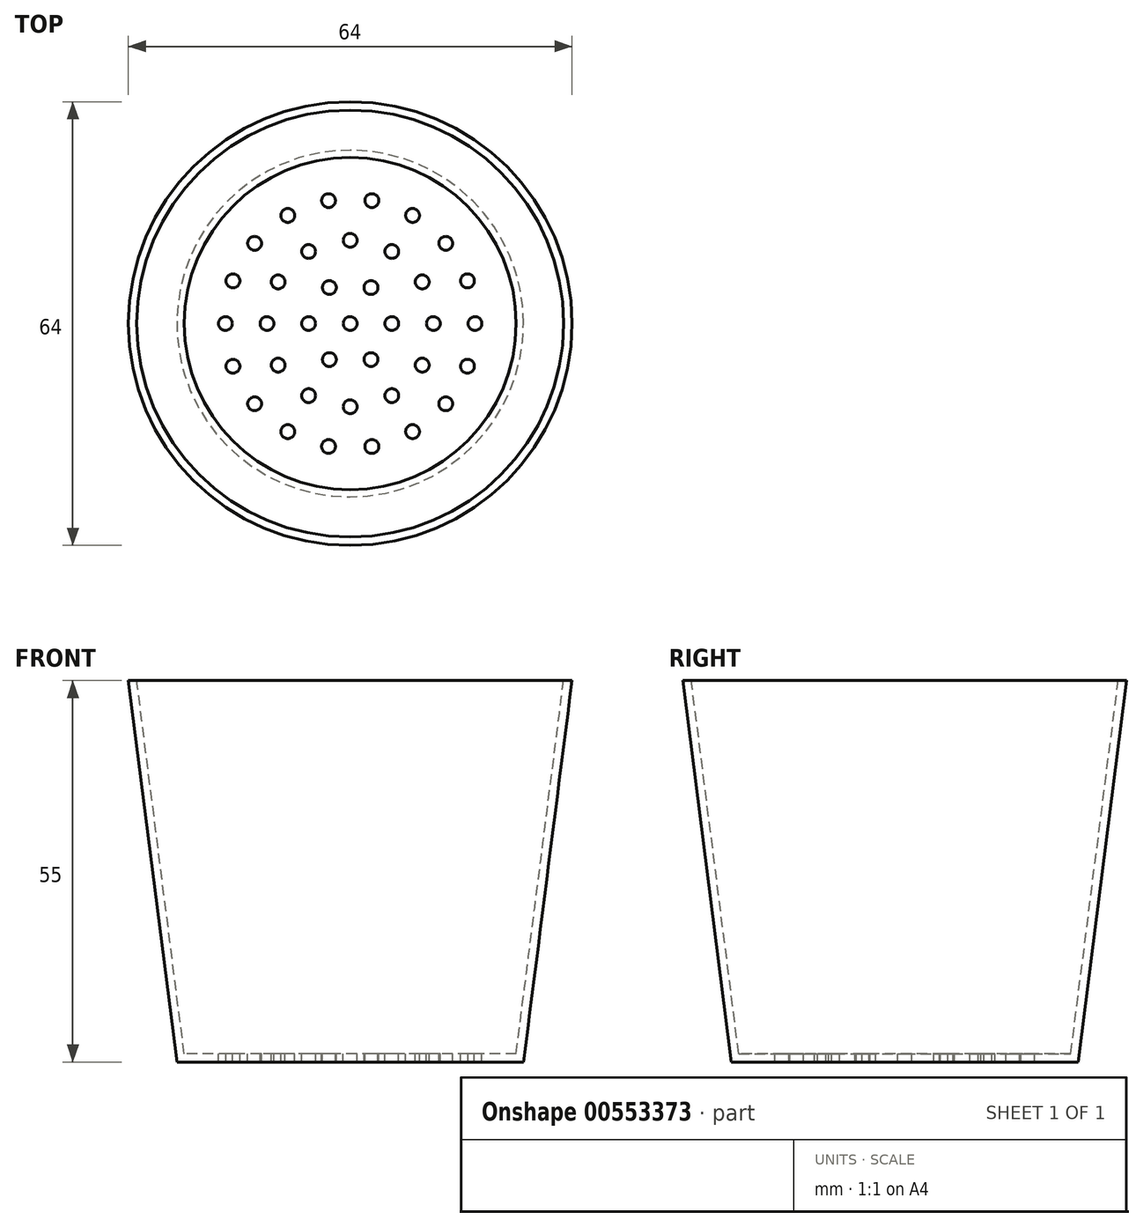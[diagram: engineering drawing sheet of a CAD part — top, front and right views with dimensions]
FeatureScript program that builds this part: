
annotation { "Feature Type Name" : "Feature", "Feature Type Description" : "" }
export const myFeature = defineFeature(function(context is Context, id is Id, definition is map)
    precondition{}
    {
        {
            var Q0;
            Q0=qCreatedBy(makeId("Front.planeOp"),FACE);
            var sketch = newSketch(context, id + "F0", { "sketchPlane" : qUnion([Q0])});
            skLineSegment(sketch, "E0", {"start": v(0, 70.08) * mm, "end": v(0, -27.51) * mm, "construction": true});
            skLineSegment(sketch, "E1", {"start": v(-32, 55) * mm, "end": v(-25, 0) * mm});
            skLineSegment(sketch, "E2", {"start": v(-25, 0) * mm, "end": v(0, 0) * mm});
            skLineSegment(sketch, "E3.0", {"start": v(-23.94, 1.2) * mm, "end": v(0, 1.2) * mm});
            skLineSegment(sketch, "E3.1", {"start": v(-30.8, 55) * mm, "end": v(-23.94, 1.2) * mm});
            skLineSegment(sketch, "E4", {"start": v(-32, 55) * mm, "end": v(-30.8, 55) * mm});
            skLineSegment(sketch, "E5", {"start": v(0, 1.2) * mm, "end": v(0, 0) * mm});
            skSolve(sketch);
        }
        {
            var Q0;
            Q0=makeQuery(id+"F0.imprint","IMPRINT",FACE,{"disambiguationData":[TD([[makeQuery(id+"F0.imprint","IMPRINT",EDGE,{"derivedFrom":sQuery(id+"F0.wireOp",EDGE,"E1")}),1.0]])]});
            var Q1;
            Q1=sQuery(id+"F0.wireOp",EDGE,"E0");
            revolve(context, id + "F1", {"entities" : qUnion([Q0]), "axis" : qUnion([Q1]), "revolveType" : RevolveType.FULL});
        }
        {
            var Q0;
            Q0=makeQuery(id+"F1.opRevolve","SWEPT_FACE",FACE,{"disambiguationData":[OSD([sQuery(id+"F0.wireOp",EDGE,"E3.0")])]});
            var sketch = newSketch(context, id + "F2", { "sketchPlane" : qUnion([Q0])});
            skCircle(sketch, "E6", {"center": v(0, 0) * mm, "radius": 1 * mm});
            skCircle(sketch, "E7", {"center": v(6, 0) * mm, "radius": 1 * mm});
            skCircle(sketch, "E8.1.0", {"center": v(3, 5.2) * mm, "radius": 1 * mm});
            skCircle(sketch, "E8.2.0", {"center": v(-3, 5.2) * mm, "radius": 1 * mm});
            skCircle(sketch, "E8.3.0", {"center": v(-6, 0) * mm, "radius": 1 * mm});
            skCircle(sketch, "E8.4.0", {"center": v(-3, -5.2) * mm, "radius": 1 * mm});
            skCircle(sketch, "E8.5.0", {"center": v(3, -5.2) * mm, "radius": 1 * mm});
            skCircle(sketch, "E9", {"center": v(12, 0) * mm, "radius": 1 * mm});
            skCircle(sketch, "E10.1.0", {"center": v(10.4, 6) * mm, "radius": 1 * mm});
            skCircle(sketch, "E10.2.0", {"center": v(6, 10.4) * mm, "radius": 1 * mm});
            skCircle(sketch, "E10.3.0", {"center": v(0, 12) * mm, "radius": 1 * mm});
            skCircle(sketch, "E10.4.0", {"center": v(-6, 10.4) * mm, "radius": 1 * mm});
            skCircle(sketch, "E10.5.0", {"center": v(-10.4, 6) * mm, "radius": 1 * mm});
            skCircle(sketch, "E10.6.0", {"center": v(-12, 0) * mm, "radius": 1 * mm});
            skCircle(sketch, "E10.7.0", {"center": v(-10.4, -6) * mm, "radius": 1 * mm});
            skCircle(sketch, "E10.8.0", {"center": v(-6, -10.4) * mm, "radius": 1 * mm});
            skCircle(sketch, "E10.9.0", {"center": v(0, -12) * mm, "radius": 1 * mm});
            skCircle(sketch, "E10.10.0", {"center": v(6, -10.4) * mm, "radius": 1 * mm});
            skCircle(sketch, "E10.11.0", {"center": v(10.4, -6) * mm, "radius": 1 * mm});
            skCircle(sketch, "E11", {"center": v(18, 0) * mm, "radius": 1 * mm});
            skCircle(sketch, "E12.1.0", {"center": v(16.91, 6.16) * mm, "radius": 1 * mm});
            skCircle(sketch, "E12.2.0", {"center": v(13.79, 11.57) * mm, "radius": 1 * mm});
            skCircle(sketch, "E12.3.0", {"center": v(9, 15.59) * mm, "radius": 1 * mm});
            skCircle(sketch, "E12.4.0", {"center": v(3.13, 17.73) * mm, "radius": 1 * mm});
            skCircle(sketch, "E12.5.0", {"center": v(-3.13, 17.73) * mm, "radius": 1 * mm});
            skCircle(sketch, "E12.6.0", {"center": v(-9, 15.59) * mm, "radius": 1 * mm});
            skCircle(sketch, "E12.7.0", {"center": v(-13.79, 11.57) * mm, "radius": 1 * mm});
            skCircle(sketch, "E12.8.0", {"center": v(-16.91, 6.16) * mm, "radius": 1 * mm});
            skCircle(sketch, "E12.9.0", {"center": v(-18, 0) * mm, "radius": 1 * mm});
            skCircle(sketch, "E12.10.0", {"center": v(-16.91, -6.16) * mm, "radius": 1 * mm});
            skCircle(sketch, "E12.11.0", {"center": v(-13.79, -11.57) * mm, "radius": 1 * mm});
            skCircle(sketch, "E12.12.0", {"center": v(-9, -15.59) * mm, "radius": 1 * mm});
            skCircle(sketch, "E12.13.0", {"center": v(-3.13, -17.73) * mm, "radius": 1 * mm});
            skCircle(sketch, "E12.14.0", {"center": v(3.13, -17.73) * mm, "radius": 1 * mm});
            skCircle(sketch, "E12.15.0", {"center": v(9, -15.59) * mm, "radius": 1 * mm});
            skCircle(sketch, "E12.16.0", {"center": v(13.79, -11.57) * mm, "radius": 1 * mm});
            skCircle(sketch, "E12.17.0", {"center": v(16.91, -6.16) * mm, "radius": 1 * mm});
            skSolve(sketch);
        }
        {
            var Q0;
            Q0 = qSketchRegion(id + "F2", true);
            extrude(context, id + "F3", {"entities" : qUnion([Q0]), "operationType" : NewBodyOperationType.REMOVE, "endBound" : BoundingType.UP_TO_NEXT, "oppositeDirection" : true, "depth" : 25 * mm, "offsetDistance" : 25 * mm});
        }
    });
